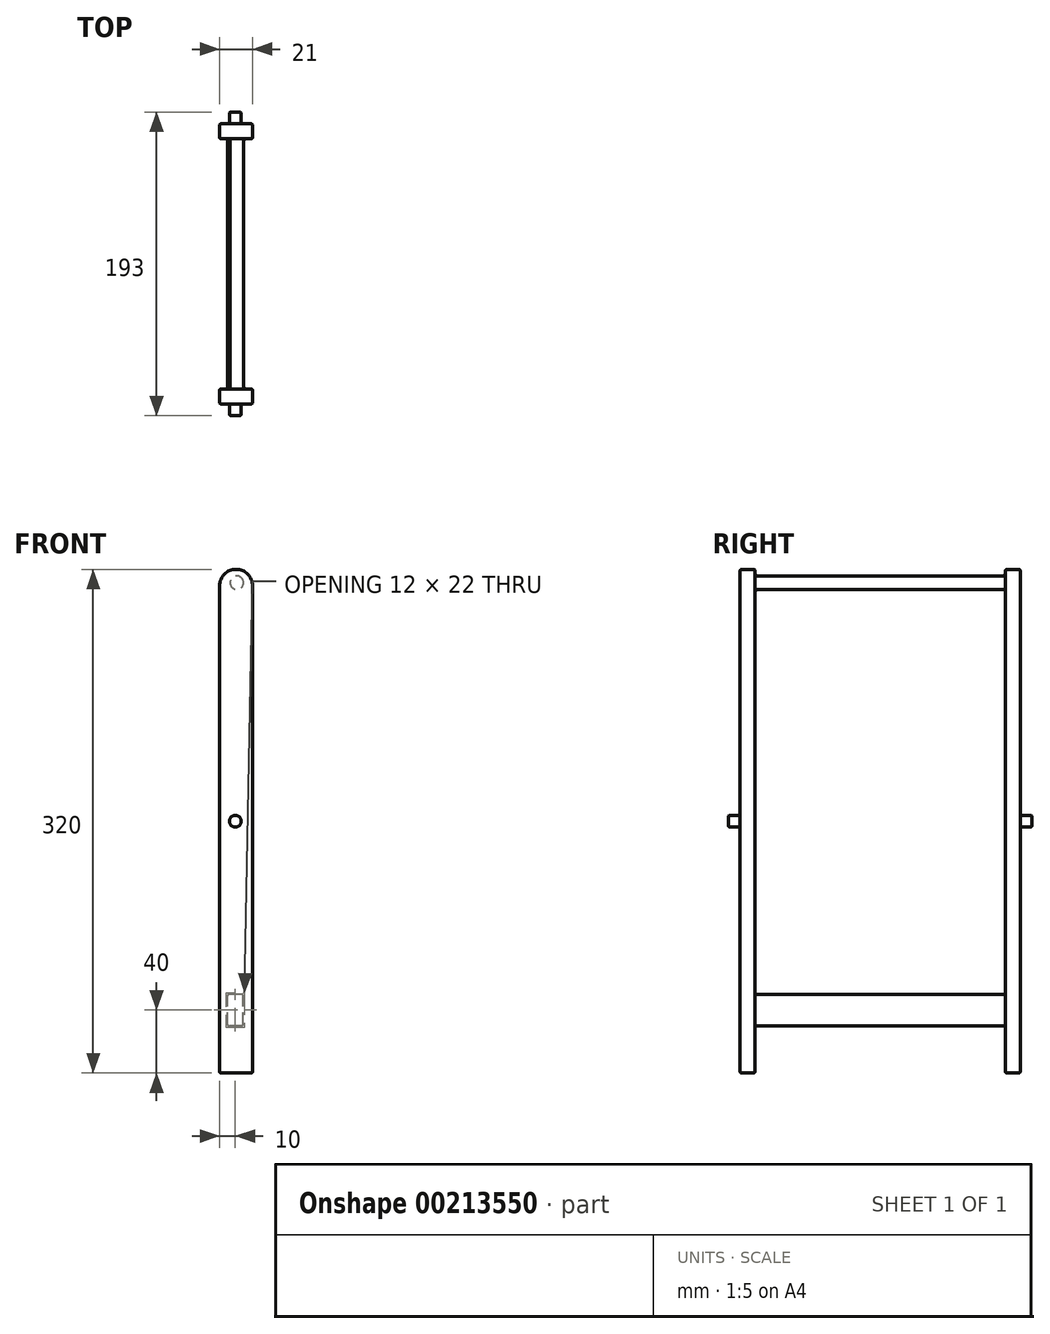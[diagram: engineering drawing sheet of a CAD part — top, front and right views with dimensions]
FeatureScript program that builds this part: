
annotation { "Feature Type Name" : "Feature", "Feature Type Description" : "" }
export const myFeature = defineFeature(function(context is Context, id is Id, definition is map)
    precondition{}
    {
        {
            var Q0;
            Q0=qCreatedBy(makeId("Front.planeOp"),FACE);
            var sketch = newSketch(context, id + "F0", { "sketchPlane" : qUnion([Q0])});
            skLineSegment(sketch, "E0.top", {"start": v(-11, -175) * mm, "end": v(10, -175) * mm});
            skLineSegment(sketch, "E0.left", {"start": v(-11, 134.5) * mm, "end": v(-11, -175) * mm});
            skLineSegment(sketch, "E0.right", {"start": v(10, 134.5) * mm, "end": v(10, -175) * mm});
            skArc(sketch, "E1", {"start": v(10, 134.5) * mm, "mid": v(-0.5, 145) * mm, "end": v(-11, 134.5) * mm});
            skSolve(sketch);
        }
        {
            var Q0;
            Q0 = qSketchRegion(id + "F0", true);
            extrude(context, id + "F1", {"entities" : qUnion([Q0]), "depth" : 9.5 * mm});
        }
        {
            var Q0;
            Q0=makeQuery(id+"F1.opExtrude","CAP_FACE",FACE,{"disambiguationData":[OSD([sQuery(id+"F0.wireOp",EDGE,"E0.top"),sQuery(id+"F0.wireOp",EDGE,"E0.left"),sQuery(id+"F0.wireOp",EDGE,"E0.right"),sQuery(id+"F0.wireOp",EDGE,"E1")])],"isStart":false});
            var sketch = newSketch(context, id + "F2", { "sketchPlane" : qUnion([Q0])});
            skLineSegment(sketch, "E2.bottom", {"start": v(4, -145) * mm, "end": v(-6, -145) * mm});
            skLineSegment(sketch, "E2.top", {"start": v(4, -125) * mm, "end": v(-6, -125) * mm});
            skLineSegment(sketch, "E2.left", {"start": v(4, -145) * mm, "end": v(4, -125) * mm});
            skLineSegment(sketch, "E2.right", {"start": v(-6, -145) * mm, "end": v(-6, -125) * mm});
            skCircle(sketch, "E3", {"center": v(0, 136.5) * mm, "radius": 4.25 * mm});
            skSolve(sketch);
        }
        {
            var Q0;
            Q0=makeQuery(id+"F2.imprint","IMPRINT",FACE,{"disambiguationData":[TD([[makeQuery(id+"F2.imprint","IMPRINT",EDGE,{"derivedFrom":sQuery(id+"F2.wireOp",EDGE,"E3")}),1.0]])]});
            var Q1;
            Q1=makeQuery(id+"F2.imprint","IMPRINT",FACE,{"disambiguationData":[TD([[makeQuery(id+"F2.imprint","IMPRINT",EDGE,{"derivedFrom":sQuery(id+"F2.wireOp",EDGE,"E2.bottom")}),-1.0]])]});
            extrude(context, id + "F3", {"entities" : qUnion([Q0, Q1]), "operationType" : NewBodyOperationType.ADD, "depth" : 159 * mm});
        }
        {
            var Q0;
            Q0=makeQuery(id+"F3.opExtrude","CAP_FACE",FACE,{"disambiguationData":[OSD([sQuery(id+"F2.wireOp",EDGE,"E2.bottom"),sQuery(id+"F2.wireOp",EDGE,"E2.top"),sQuery(id+"F2.wireOp",EDGE,"E2.left"),sQuery(id+"F2.wireOp",EDGE,"E2.right")])],"isStart":false});
            var sketch = newSketch(context, id + "F4", { "sketchPlane" : qUnion([Q0])});
            skLineSegment(sketch, "E4.bottom", {"start": v(-11, -175) * mm, "end": v(10, -175) * mm});
            skLineSegment(sketch, "E4.left", {"start": v(-11, -175) * mm, "end": v(-11, 134.5) * mm});
            skLineSegment(sketch, "E4.right", {"start": v(10, -175) * mm, "end": v(10, 134.5) * mm});
            skArc(sketch, "E5", {"start": v(10, 134.5) * mm, "mid": v(-0.5, 145) * mm, "end": v(-11, 134.5) * mm});
            skSolve(sketch);
        }
        {
            var Q0;
            Q0=makeQuery(id+"F4.imprint","IMPRINT",FACE,{"disambiguationData":[TD([[makeQuery(id+"F4.imprint","IMPRINT",EDGE,{"derivedFrom":sQuery(id+"F4.wireOp",EDGE,"E4.bottom")}),1.0]])]});
            var Q1;
            Q1=makeQuery(id+"F4.imprint","IMPRINT",FACE,{"disambiguationData":[TD([[makeQuery(id+"F4.imprint","IMPRINT",EDGE,{"derivedFrom":makeQuery(id+"F3.opExtrude","CAP_EDGE",EDGE,{"disambiguationData":[OSD([sQuery(id+"F2.wireOp",EDGE,"E2.bottom")])],"isStart":false})}),-1.0]])]});
            extrude(context, id + "F5", {"entities" : qUnion([Q0, Q1]), "operationType" : NewBodyOperationType.ADD, "depth" : 9.5 * mm});
        }
        {
            var Q0;
            Q0=makeQuery(id+"F5.opExtrude","CAP_FACE",FACE,{"disambiguationData":[OSD([sQuery(id+"F4.wireOp",EDGE,"E4.bottom"),sQuery(id+"F4.wireOp",EDGE,"E4.left"),sQuery(id+"F4.wireOp",EDGE,"E4.right"),sQuery(id+"F4.wireOp",EDGE,"E5")])],"isStart":false});
            var sketch = newSketch(context, id + "F6", { "sketchPlane" : qUnion([Q0])});
            skCircle(sketch, "E6", {"center": v(-1, -15) * mm, "radius": 3.75 * mm});
            skSolve(sketch);
        }
        {
            var Q0;
            Q0=makeQuery(id+"F0.imprint","IMPRINT",FACE,{"disambiguationData":[TD([[makeQuery(id+"F0.imprint","IMPRINT",EDGE,{"derivedFrom":sQuery(id+"F0.wireOp",EDGE,"E0.top")}),1.0]])]});
            var sketch = newSketch(context, id + "F7", { "sketchPlane" : qUnion([Q0])});
            skCircle(sketch, "E7", {"center": v(-1, -15) * mm, "radius": 3.75 * mm});
            skSolve(sketch);
        }
        {
            var Q0;
            Q0 = qSketchRegion(id + "F6", true);
            var Q1;
            Q1 = qSketchRegion(id + "F7", true);
            extrude(context, id + "F8", {"entities" : qUnion([Q0, Q1]), "operationType" : NewBodyOperationType.ADD, "endBound" : BoundingType.SYMMETRIC, "depth" : 15 * mm});
        }
        {
            var Q0;
            Q0=makeQuery(id+"F8.opExtrude","SWEPT_FACE",FACE,{"disambiguationData":[OSD([sQuery(id+"F7.wireOp",EDGE,"E7")])]});
            var Q1;
            Q1=makeQuery(id+"F8.opExtrude","SWEPT_FACE",FACE,{"disambiguationData":[OSD([sQuery(id+"F6.wireOp",EDGE,"E6")])]});
            fillet(context, id + "F9", {"entities" : qUnion([Q0, Q1]), "radius" : 1 * mm, "tangentPropagation" : true, "allowEdgeOverflow" : false});
        }
        {
            var Q0;
            Q0=makeQuery(id+"F3.opExtrude","CAP_EDGE",EDGE,{"disambiguationData":[OSD([sQuery(id+"F2.wireOp",EDGE,"E2.right")])],"isStart":true});
            var Q1;
            Q1=makeQuery(id+"F3.opExtrude","CAP_EDGE",EDGE,{"disambiguationData":[OSD([sQuery(id+"F2.wireOp",EDGE,"E2.left")])],"isStart":true});
            var Q2;
            Q2=makeQuery(id+"F3.opExtrude","CAP_EDGE",EDGE,{"disambiguationData":[OSD([sQuery(id+"F2.wireOp",EDGE,"E2.bottom")])],"isStart":true});
            var Q3;
            Q3=makeQuery(id+"F3.opExtrude","CAP_EDGE",EDGE,{"disambiguationData":[OSD([sQuery(id+"F2.wireOp",EDGE,"E2.top")])],"isStart":true});
            var Q4;
            Q4=makeQuery(id+"F3.opExtrude","CAP_EDGE",EDGE,{"disambiguationData":[OSD([sQuery(id+"F2.wireOp",EDGE,"E2.top")])],"isStart":false});
            var Q5;
            Q5=makeQuery(id+"F3.opExtrude","CAP_EDGE",EDGE,{"disambiguationData":[OSD([sQuery(id+"F2.wireOp",EDGE,"E2.right")])],"isStart":false});
            var Q6;
            Q6=makeQuery(id+"F3.opExtrude","SWEPT_FACE",FACE,{"disambiguationData":[OSD([sQuery(id+"F2.wireOp",EDGE,"E3")])]});
            var Q7;
            Q7=makeQuery(id+"F3.opExtrude","CAP_EDGE",EDGE,{"disambiguationData":[OSD([sQuery(id+"F2.wireOp",EDGE,"E2.left")])],"isStart":false});
            var Q8;
            Q8=makeQuery(id+"F3.opExtrude","CAP_EDGE",EDGE,{"disambiguationData":[OSD([sQuery(id+"F2.wireOp",EDGE,"E2.bottom")])],"isStart":false});
            fillet(context, id + "F10", {"entities" : qUnion([Q0, Q1, Q2, Q3, Q4, Q5, Q6, Q7, Q8]), "radius" : 2 * mm, "tangentPropagation" : true, "allowEdgeOverflow" : false});
        }
        {
            var Q0;
            Q0=makeQuery(id+"F1.opExtrude","SWEPT_FACE",FACE,{"disambiguationData":[OSD([sQuery(id+"F0.wireOp",EDGE,"E0.top")])]});
            var Q1;
            Q1=makeQuery(id+"F5.opExtrude","SWEPT_FACE",FACE,{"disambiguationData":[OSD([sQuery(id+"F4.wireOp",EDGE,"E4.bottom")])]});
            var Q2;
            Q2=makeQuery(id+"F1.opExtrude","CAP_FACE",FACE,{"disambiguationData":[OSD([sQuery(id+"F0.wireOp",EDGE,"E0.top"),sQuery(id+"F0.wireOp",EDGE,"E0.left"),sQuery(id+"F0.wireOp",EDGE,"E0.right"),sQuery(id+"F0.wireOp",EDGE,"E1")])],"isStart":true});
            var Q3;
            Q3=makeQuery(id+"F5.opExtrude","CAP_FACE",FACE,{"disambiguationData":[OSD([sQuery(id+"F4.wireOp",EDGE,"E4.bottom"),sQuery(id+"F4.wireOp",EDGE,"E4.left"),sQuery(id+"F4.wireOp",EDGE,"E4.right"),sQuery(id+"F4.wireOp",EDGE,"E5")])],"isStart":false});
            var Q4;
            Q4=makeQuery(id+"F5.opExtrude","SWEPT_FACE",FACE,{"disambiguationData":[OSD([sQuery(id+"F4.wireOp",EDGE,"E4.left")])]});
            var Q5;
            Q5=makeQuery(id+"F1.opExtrude","SWEPT_FACE",FACE,{"disambiguationData":[OSD([sQuery(id+"F0.wireOp",EDGE,"E0.left")])]});
            var Q6;
            Q6=makeQuery(id+"F3.opExtrude","SWEPT_FACE",FACE,{"disambiguationData":[OSD([sQuery(id+"F2.wireOp",EDGE,"E2.right")])]});
            var Q7;
            Q7=makeQuery(id+"F3.opExtrude","SWEPT_FACE",FACE,{"disambiguationData":[OSD([sQuery(id+"F2.wireOp",EDGE,"E2.bottom")])]});
            var Q8;
            Q8=makeQuery(id+"F3.opExtrude","SWEPT_FACE",FACE,{"disambiguationData":[OSD([sQuery(id+"F2.wireOp",EDGE,"E2.left")])]});
            var Q9;
            Q9=makeQuery(id+"F3.opExtrude","SWEPT_FACE",FACE,{"disambiguationData":[OSD([sQuery(id+"F2.wireOp",EDGE,"E2.top")])]});
            fillet(context, id + "F11", {"entities" : qUnion([Q0, Q1, Q2, Q3, Q4, Q5, Q6, Q7, Q8, Q9]), "radius" : 1 * mm, "tangentPropagation" : true, "allowEdgeOverflow" : false});
        }
    });
